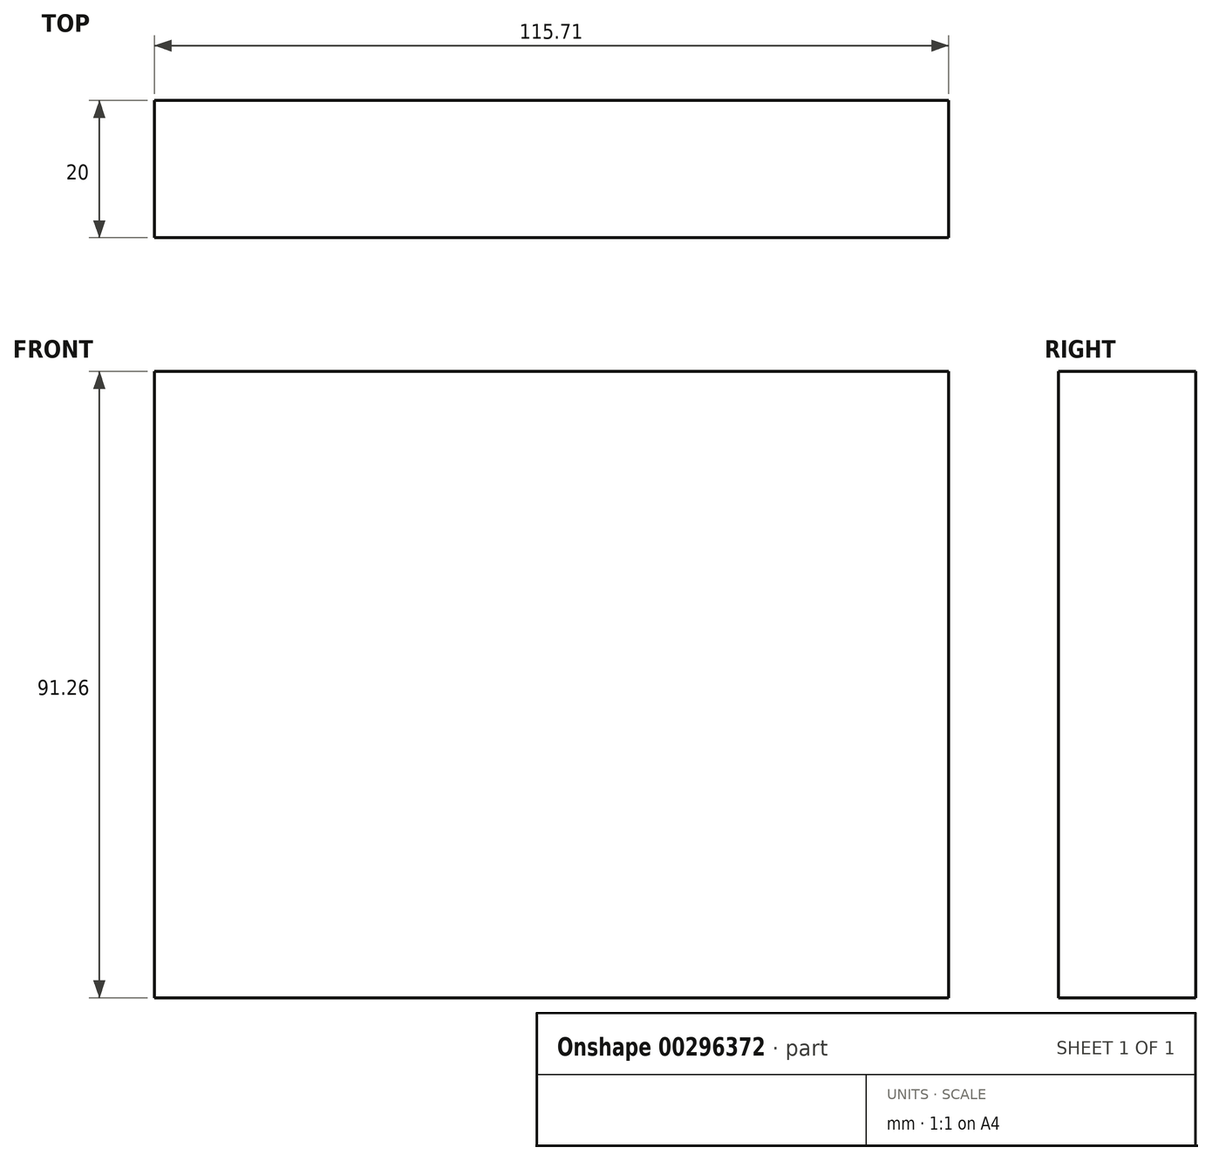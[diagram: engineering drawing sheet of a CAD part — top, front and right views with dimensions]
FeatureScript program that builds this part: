
annotation { "Feature Type Name" : "Feature", "Feature Type Description" : "" }
export const myFeature = defineFeature(function(context is Context, id is Id, definition is map)
    precondition{}
    {
        {
            var Q0;
            Q0=qCreatedBy(makeId("Front.planeOp"),FACE);
            var sketch = newSketch(context, id + "F0", { "sketchPlane" : qUnion([Q0])});
            skLineSegment(sketch, "E0.bottom", {"start": v(-58.2, 47.9) * mm, "end": v(57.5, 47.9) * mm});
            skLineSegment(sketch, "E0.top", {"start": v(-58.2, -43.37) * mm, "end": v(57.5, -43.37) * mm});
            skLineSegment(sketch, "E0.left", {"start": v(-58.2, 47.9) * mm, "end": v(-58.2, -43.37) * mm});
            skLineSegment(sketch, "E0.right", {"start": v(57.5, 47.9) * mm, "end": v(57.5, -43.37) * mm});
            skSolve(sketch);
        }
        {
            var Q0;
            Q0 = qSketchRegion(id + "F0", true);
            extrude(context, id + "F1", {"entities" : qUnion([Q0]), "depth" : 10 * mm});
        }
        {
            var Q0;
            Q0=makeQuery(id+"F1.opExtrude","SWEPT_BODY",BODY,{"disambiguationData":[OSD([sQuery(id+"F0.wireOp",EDGE,"E0.bottom"),sQuery(id+"F0.wireOp",EDGE,"E0.top"),sQuery(id+"F0.wireOp",EDGE,"E0.left"),sQuery(id+"F0.wireOp",EDGE,"E0.right")])]});
            var Q1;
            Q1=makeQuery(id+"F1.opExtrude","CAP_FACE",FACE,{"disambiguationData":[OSD([sQuery(id+"F0.wireOp",EDGE,"E0.bottom"),sQuery(id+"F0.wireOp",EDGE,"E0.top"),sQuery(id+"F0.wireOp",EDGE,"E0.left"),sQuery(id+"F0.wireOp",EDGE,"E0.right")])],"isStart":true});
            mirror(context, id + "F2", {"operationType" : NewBodyOperationType.ADD, "entities" : qUnion([Q0]), "mirrorPlane" : qUnion([Q1])});
        }
    });
